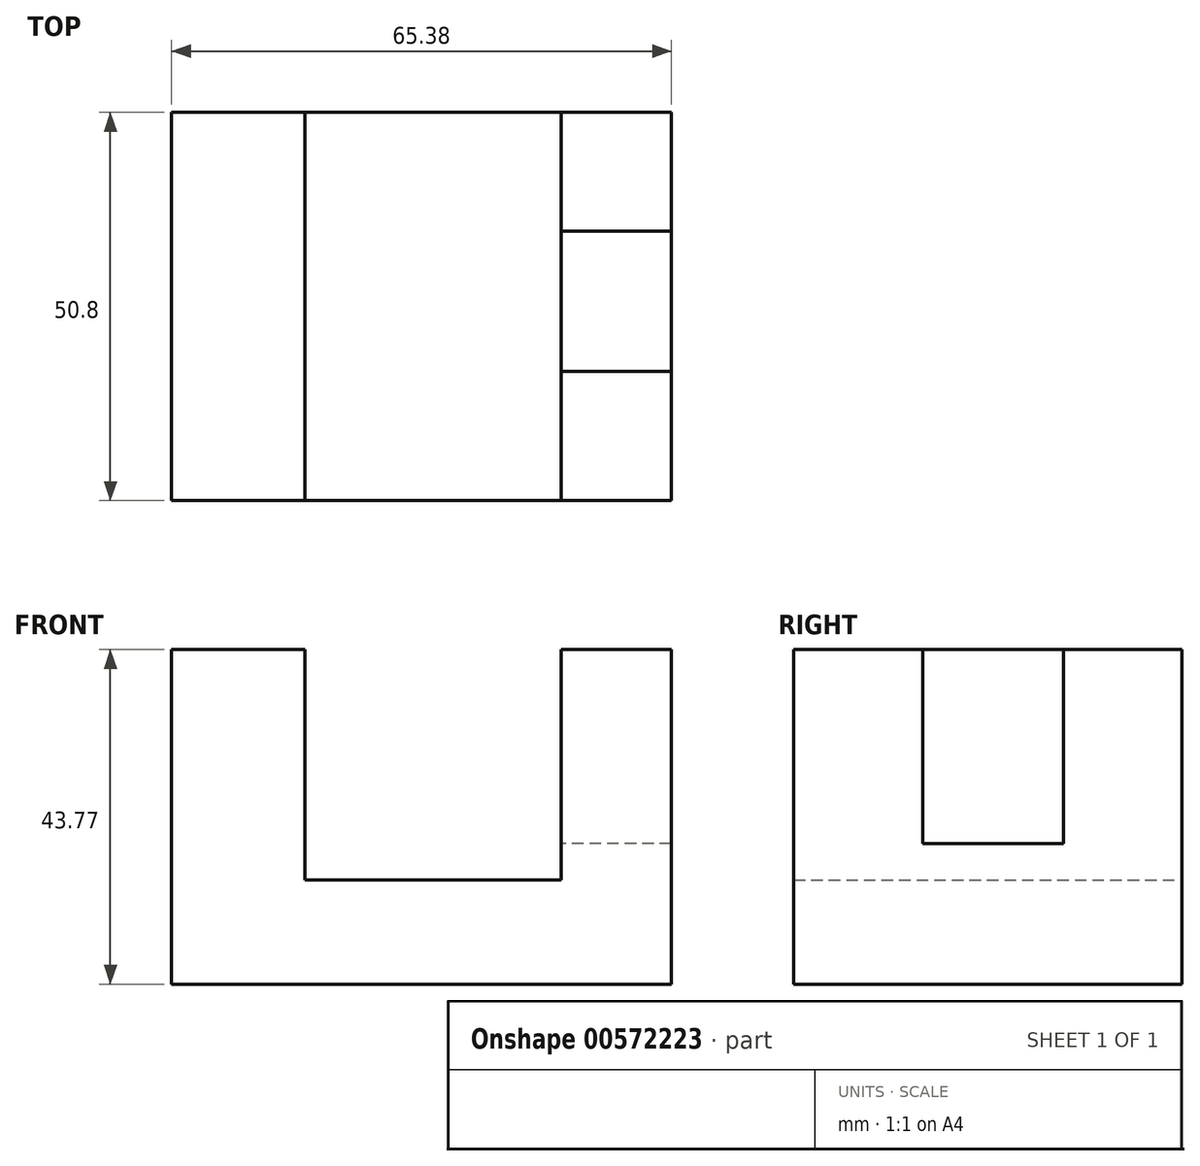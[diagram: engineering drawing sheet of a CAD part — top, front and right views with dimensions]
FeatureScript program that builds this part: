
annotation { "Feature Type Name" : "Feature", "Feature Type Description" : "" }
export const myFeature = defineFeature(function(context is Context, id is Id, definition is map)
    precondition{}
    {
        {
            var Q0;
            Q0=qCreatedBy(makeId("Front.planeOp"),FACE);
            var sketch = newSketch(context, id + "F0", { "sketchPlane" : qUnion([Q0])});
            skLineSegment(sketch, "E0.bottom", {"start": v(0, 0) * mm, "end": v(65.38, 0) * mm});
            skLineSegment(sketch, "E0.top", {"start": v(0, 43.77) * mm, "end": v(17.42, 43.77) * mm});
            skLineSegment(sketch, "E0.left", {"start": v(0, 0) * mm, "end": v(0, 43.77) * mm});
            skLineSegment(sketch, "E0.right", {"start": v(65.38, 0) * mm, "end": v(65.38, 43.77) * mm});
            skLineSegment(sketch, "E1.top", {"start": v(17.42, 13.66) * mm, "end": v(50.97, 13.66) * mm});
            skLineSegment(sketch, "E1.left", {"start": v(17.42, 43.77) * mm, "end": v(17.42, 13.66) * mm});
            skLineSegment(sketch, "E1.right", {"start": v(50.97, 43.77) * mm, "end": v(50.97, 13.66) * mm});
            skLineSegment(sketch, "E2.trimOffspring", {"start": v(50.97, 43.77) * mm, "end": v(65.38, 43.77) * mm});
            skSolve(sketch);
        }
        {
            var Q0;
            Q0 = qSketchRegion(id + "F0", true);
            var Q1;
            Q1=makeQuery(id+"F0.imprint","IMPRINT",FACE,{"disambiguationData":[TD([[makeQuery(id+"F0.imprint","IMPRINT",EDGE,{"derivedFrom":sQuery(id+"F0.wireOp",EDGE,"E0.bottom")}),1.0]])]});
            extrude(context, id + "F1", {"entities" : qUnion([Q0, Q1]), "depth" : 50.8 * mm, "offsetDistance" : 25.4 * mm});
        }
        {
            var Q0;
            Q0=makeQuery(id+"F1.opExtrude","SWEPT_FACE",FACE,{"disambiguationData":[OSD([sQuery(id+"F0.wireOp",EDGE,"E2.trimOffspring")])]});
            var sketch = newSketch(context, id + "F2", { "sketchPlane" : qUnion([Q0])});
            skLineSegment(sketch, "E3.bottom", {"start": v(65.38, -33.88) * mm, "end": v(50.97, -33.88) * mm});
            skLineSegment(sketch, "E3.top", {"start": v(65.38, -15.52) * mm, "end": v(50.97, -15.52) * mm});
            skLineSegment(sketch, "E3.left", {"start": v(65.38, -33.88) * mm, "end": v(65.38, -15.52) * mm});
            skLineSegment(sketch, "E3.right", {"start": v(50.97, -33.88) * mm, "end": v(50.97, -15.52) * mm});
            skSolve(sketch);
        }
        {
            var Q0;
            Q0 = qSketchRegion(id + "F2", true);
            extrude(context, id + "F3", {"entities" : qUnion([Q0]), "operationType" : NewBodyOperationType.REMOVE, "oppositeDirection" : true, "depth" : 25.4 * mm, "offsetDistance" : 25.4 * mm});
        }
    });
